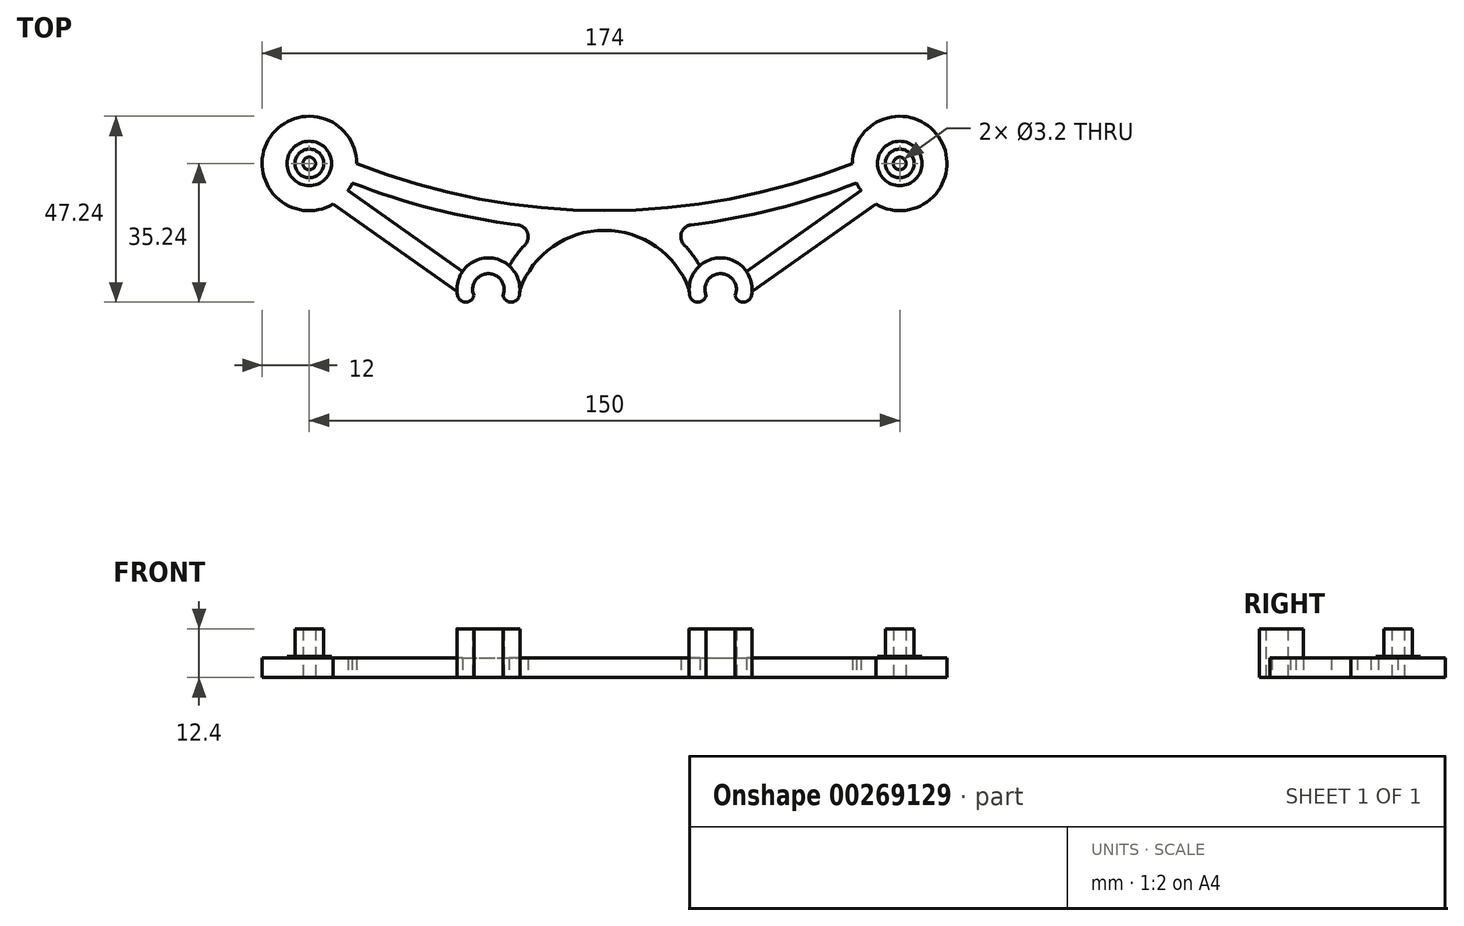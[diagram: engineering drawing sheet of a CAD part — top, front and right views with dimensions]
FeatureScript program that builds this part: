
annotation { "Feature Type Name" : "Feature", "Feature Type Description" : "" }
export const myFeature = defineFeature(function(context is Context, id is Id, definition is map)
    precondition{}
    {
        {
            var Q0;
            Q0=qCreatedBy(makeId("Top.planeOp"),FACE);
            var sketch = newSketch(context, id + "F0", { "sketchPlane" : qUnion([Q0])});
            skCircle(sketch, "E0", {"center": v(-75, 32) * mm, "radius": 1.6 * mm});
            skCircle(sketch, "E1", {"center": v(75, 32) * mm, "radius": 1.6 * mm});
            skCircle(sketch, "E2", {"center": v(29.5, 0) * mm, "radius": 4 * mm, "construction": true});
            skCircle(sketch, "E3", {"center": v(-29.5, 0) * mm, "radius": 4 * mm, "construction": true});
            skLineSegment(sketch, "E4", {"start": v(-29.5, 0) * mm, "end": v(29.5, 0) * mm, "construction": true});
            skPoint(sketch, "E5", {"position": v(0, 0) * mm});
            skLineSegment(sketch, "E6", {"start": v(-75, 32) * mm, "end": v(75, 32) * mm, "construction": true});
            skPoint(sketch, "E7", {"position": v(0, 32) * mm});
            skCircle(sketch, "E8", {"center": v(-75, 32) * mm, "radius": 3.65 * mm, "construction": true});
            skCircle(sketch, "E9", {"center": v(75, 32) * mm, "radius": 3.65 * mm, "construction": true});
            skCircle(sketch, "E10", {"center": v(75, 32) * mm, "radius": 12 * mm, "construction": true});
            skCircle(sketch, "E11", {"center": v(-75, 32) * mm, "radius": 12 * mm, "construction": true});
            skArc(sketch, "E12", {"start": v(-33.2, -1.53) * mm, "mid": v(-29.5, 4) * mm, "end": v(-25.8, -1.53) * mm});
            skLineSegment(sketch, "E13", {"start": v(-33.2, -1.53) * mm, "end": v(-25.8, -1.53) * mm, "construction": true});
            skArc(sketch, "E14", {"start": v(25.8, -1.53) * mm, "mid": v(29.5, 4) * mm, "end": v(33.2, -1.53) * mm});
            skLineSegment(sketch, "E15", {"start": v(25.8, -1.53) * mm, "end": v(33.2, -1.53) * mm, "construction": true});
            skArc(sketch, "E16", {"start": v(-37.35, -1.53) * mm, "mid": v(-29.5, 8) * mm, "end": v(-21.65, -1.53) * mm, "construction": true});
            skPoint(sketch, "E16.startSnap0", {"position": v(-29.5, -1.53) * mm});
            skArc(sketch, "E17", {"start": v(21.65, -1.53) * mm, "mid": v(29.5, 8) * mm, "end": v(37.35, -1.53) * mm, "construction": true});
            skArc(sketch, "E18", {"start": v(-37.35, -1.53) * mm, "mid": v(-35.27, -3.24) * mm, "end": v(-33.2, -1.53) * mm});
            skArc(sketch, "E19", {"start": v(-21.65, -1.53) * mm, "mid": v(-23.73, -3.24) * mm, "end": v(-25.8, -1.53) * mm});
            skArc(sketch, "E20", {"start": v(21.65, -1.53) * mm, "mid": v(23.73, -3.24) * mm, "end": v(25.8, -1.53) * mm});
            skArc(sketch, "E21", {"start": v(37.35, -1.53) * mm, "mid": v(35.27, -3.24) * mm, "end": v(33.2, -1.53) * mm});
            skArc(sketch, "E22", {"start": v(-63, 32) * mm, "mid": v(0, 20) * mm, "end": v(63, 32) * mm});
            skArc(sketch, "E23", {"start": v(21.5, 0) * mm, "mid": v(0, 15) * mm, "end": v(-21.5, 0) * mm});
            skArc(sketch, "E24.0", {"start": v(-64.07, 27.05) * mm, "mid": v(-43.37, 20.42) * mm, "end": v(-22.01, 16.38) * mm});
            skLineSegment(sketch, "E25", {"start": v(-37.48, -0.5) * mm, "end": v(37.48, -0.5) * mm, "construction": true});
            skLineSegment(sketch, "E26", {"start": v(-75, 20) * mm, "end": v(75, 20) * mm, "construction": true});
            skArc(sketch, "E27.trimOffspring", {"start": v(-20.21, 11.33) * mm, "mid": v(-22.37, 8.78) * mm, "end": v(-24.2, 6) * mm});
            skArc(sketch, "E28.trimOffspring", {"start": v(22.01, 16.38) * mm, "mid": v(43.37, 20.42) * mm, "end": v(64.07, 27.05) * mm});
            skArc(sketch, "E29.filletArc", {"start": v(22.01, 16.38) * mm, "mid": v(19.56, 14.4) * mm, "end": v(20.21, 11.33) * mm});
            skArc(sketch, "E30.filletArc", {"start": v(-20.21, 11.33) * mm, "mid": v(-19.56, 14.4) * mm, "end": v(-22.01, 16.38) * mm});
            skArc(sketch, "E31", {"start": v(63, 32) * mm, "mid": v(83.49, 40.49) * mm, "end": v(75, 20) * mm});
            skArc(sketch, "E32", {"start": v(-63, 32) * mm, "mid": v(-83.49, 40.49) * mm, "end": v(-75, 20) * mm});
            skArc(sketch, "E33", {"start": v(-37.35, -1.53) * mm, "mid": v(-37.44, -1.02) * mm, "end": v(-37.48, -0.5) * mm});
            skArc(sketch, "E34", {"start": v(37.35, -1.53) * mm, "mid": v(37.44, -1.02) * mm, "end": v(37.48, -0.5) * mm});
            skArc(sketch, "E35", {"start": v(36.04, 4.6) * mm, "mid": v(30.43, 7.95) * mm, "end": v(24.2, 6) * mm});
            skArc(sketch, "E36", {"start": v(21.5, 0) * mm, "mid": v(21.54, -0.77) * mm, "end": v(21.65, -1.53) * mm});
            skArc(sketch, "E37", {"start": v(-36.04, 4.6) * mm, "mid": v(-30.43, 7.95) * mm, "end": v(-24.2, 6) * mm});
            skArc(sketch, "E38", {"start": v(-21.5, 0) * mm, "mid": v(-21.54, -0.77) * mm, "end": v(-21.65, -1.53) * mm});
            skArc(sketch, "E39.trimOffspring", {"start": v(24.2, 6) * mm, "mid": v(22.37, 8.78) * mm, "end": v(20.21, 11.33) * mm});
            skLineSegment(sketch, "E40", {"start": v(25.8, -1.53) * mm, "end": v(29.5, 0) * mm, "construction": true});
            skLineSegment(sketch, "E41", {"start": v(33.2, -1.53) * mm, "end": v(29.5, 0) * mm, "construction": true});
            skLineSegment(sketch, "E42", {"start": v(37.48, -0.5) * mm, "end": v(68.95, 21.63) * mm});
            skLineSegment(sketch, "E43", {"start": v(-37.48, -0.5) * mm, "end": v(-68.95, 21.63) * mm});
            skArc(sketch, "E44", {"start": v(-68.95, 21.63) * mm, "mid": v(-71.87, 20.42) * mm, "end": v(-75, 20) * mm});
            skArc(sketch, "E45", {"start": v(75, 20) * mm, "mid": v(71.87, 20.42) * mm, "end": v(68.95, 21.63) * mm});
            skLineSegment(sketch, "E46", {"start": v(75, 32) * mm, "end": v(29.5, 0) * mm, "construction": true});
            skLineSegment(sketch, "E47", {"start": v(65.18, 25.1) * mm, "end": v(36.04, 4.6) * mm});
            skLineSegment(sketch, "E48", {"start": v(-36.04, 4.6) * mm, "end": v(-65.18, 25.1) * mm});
            skLineSegment(sketch, "E49", {"start": v(-75, 32) * mm, "end": v(-29.5, 0) * mm, "construction": true});
            skArc(sketch, "E50", {"start": v(-64.07, 27.05) * mm, "mid": v(-64.58, 26.05) * mm, "end": v(-65.18, 25.1) * mm});
            skArc(sketch, "E51", {"start": v(65.18, 25.1) * mm, "mid": v(64.58, 26.05) * mm, "end": v(64.07, 27.05) * mm});
            skSolve(sketch);
        }
        {
            var Q0;
            Q0 = qSketchRegion(id + "F0", true);
            extrude(context, id + "F1", {"entities" : qUnion([Q0]), "depth" : 5 * mm});
        }
        {
            var Q0;
            Q0=makeQuery(id+"F1.opExtrude","CAP_FACE",FACE,{"disambiguationData":[OSD([sQuery(id+"F0.wireOp",EDGE,"E0"),sQuery(id+"F0.wireOp",EDGE,"E1"),sQuery(id+"F0.wireOp",EDGE,"E12"),sQuery(id+"F0.wireOp",EDGE,"E14"),sQuery(id+"F0.wireOp",EDGE,"E18"),sQuery(id+"F0.wireOp",EDGE,"E19"),sQuery(id+"F0.wireOp",EDGE,"E20"),sQuery(id+"F0.wireOp",EDGE,"E21"),sQuery(id+"F0.wireOp",EDGE,"E22"),sQuery(id+"F0.wireOp",EDGE,"E23"),sQuery(id+"F0.wireOp",EDGE,"E24.0"),sQuery(id+"F0.wireOp",EDGE,"E27.trimOffspring"),sQuery(id+"F0.wireOp",EDGE,"E28.trimOffspring"),sQuery(id+"F0.wireOp",EDGE,"E29.filletArc"),sQuery(id+"F0.wireOp",EDGE,"E30.filletArc"),sQuery(id+"F0.wireOp",EDGE,"E31"),sQuery(id+"F0.wireOp",EDGE,"E32"),sQuery(id+"F0.wireOp",EDGE,"E33"),sQuery(id+"F0.wireOp",EDGE,"E34"),sQuery(id+"F0.wireOp",EDGE,"E35"),sQuery(id+"F0.wireOp",EDGE,"E36"),sQuery(id+"F0.wireOp",EDGE,"E37"),sQuery(id+"F0.wireOp",EDGE,"E38"),sQuery(id+"F0.wireOp",EDGE,"E39.trimOffspring"),sQuery(id+"F0.wireOp",EDGE,"E42"),sQuery(id+"F0.wireOp",EDGE,"E43"),sQuery(id+"F0.wireOp",EDGE,"E44"),sQuery(id+"F0.wireOp",EDGE,"E45"),sQuery(id+"F0.wireOp",EDGE,"E47"),sQuery(id+"F0.wireOp",EDGE,"E48"),sQuery(id+"F0.wireOp",EDGE,"E50"),sQuery(id+"F0.wireOp",EDGE,"E51")])],"isStart":false});
            var sketch = newSketch(context, id + "F2", { "sketchPlane" : qUnion([Q0])});
            skCircle(sketch, "E52", {"center": v(-75, 32) * mm, "radius": 3.65 * mm, "construction": true});
            skCircle(sketch, "E53", {"center": v(75, 32) * mm, "radius": 3.65 * mm, "construction": true});
            skCircle(sketch, "E54", {"center": v(-75, 32) * mm, "radius": 1.6 * mm});
            skCircle(sketch, "E55", {"center": v(75, 32) * mm, "radius": 1.6 * mm});
            skCircle(sketch, "E56", {"center": v(-75, 32) * mm, "radius": 5.65 * mm});
            skCircle(sketch, "E57", {"center": v(75, 32) * mm, "radius": 5.65 * mm});
            skSolve(sketch);
        }
        {
            var Q0;
            Q0 = qSketchRegion(id + "F2", true);
            extrude(context, id + "F3", {"entities" : qUnion([Q0]), "operationType" : NewBodyOperationType.ADD, "depth" : .4 * mm});
        }
        {
            var Q0;
            Q0=makeQuery(id+"F3.opExtrude","CAP_FACE",FACE,{"disambiguationData":[OSD([sQuery(id+"F2.wireOp",EDGE,"E54"),sQuery(id+"F2.wireOp",EDGE,"E56")])],"isStart":false});
            var sketch = newSketch(context, id + "F4", { "sketchPlane" : qUnion([Q0])});
            skCircle(sketch, "E58", {"center": v(-75, 32) * mm, "radius": 1.6 * mm});
            skCircle(sketch, "E59", {"center": v(-75, 32) * mm, "radius": 3.65 * mm});
            skCircle(sketch, "E60", {"center": v(75, 32) * mm, "radius": 1.6 * mm});
            skCircle(sketch, "E61", {"center": v(75, 32) * mm, "radius": 3.65 * mm});
            skSolve(sketch);
        }
        {
            var Q0;
            Q0 = qSketchRegion(id + "F4", true);
            extrude(context, id + "F5", {"entities" : qUnion([Q0]), "operationType" : NewBodyOperationType.ADD, "depth" : 7 * mm});
        }
        {
            var Q0;
            Q0=makeQuery(id+"F1.opExtrude","CAP_FACE",FACE,{"disambiguationData":[OSD([sQuery(id+"F0.wireOp",EDGE,"E0"),sQuery(id+"F0.wireOp",EDGE,"E1"),sQuery(id+"F0.wireOp",EDGE,"E12"),sQuery(id+"F0.wireOp",EDGE,"E14"),sQuery(id+"F0.wireOp",EDGE,"E18"),sQuery(id+"F0.wireOp",EDGE,"E19"),sQuery(id+"F0.wireOp",EDGE,"E20"),sQuery(id+"F0.wireOp",EDGE,"E21"),sQuery(id+"F0.wireOp",EDGE,"E22"),sQuery(id+"F0.wireOp",EDGE,"E23"),sQuery(id+"F0.wireOp",EDGE,"E24.0"),sQuery(id+"F0.wireOp",EDGE,"E27.trimOffspring"),sQuery(id+"F0.wireOp",EDGE,"E28.trimOffspring"),sQuery(id+"F0.wireOp",EDGE,"E29.filletArc"),sQuery(id+"F0.wireOp",EDGE,"E30.filletArc"),sQuery(id+"F0.wireOp",EDGE,"E31"),sQuery(id+"F0.wireOp",EDGE,"E32"),sQuery(id+"F0.wireOp",EDGE,"E33"),sQuery(id+"F0.wireOp",EDGE,"E34"),sQuery(id+"F0.wireOp",EDGE,"E35"),sQuery(id+"F0.wireOp",EDGE,"E36"),sQuery(id+"F0.wireOp",EDGE,"E37"),sQuery(id+"F0.wireOp",EDGE,"E38"),sQuery(id+"F0.wireOp",EDGE,"E39.trimOffspring"),sQuery(id+"F0.wireOp",EDGE,"E42"),sQuery(id+"F0.wireOp",EDGE,"E43"),sQuery(id+"F0.wireOp",EDGE,"E44"),sQuery(id+"F0.wireOp",EDGE,"E45"),sQuery(id+"F0.wireOp",EDGE,"E47"),sQuery(id+"F0.wireOp",EDGE,"E48"),sQuery(id+"F0.wireOp",EDGE,"E50"),sQuery(id+"F0.wireOp",EDGE,"E51")])],"isStart":false});
            var sketch = newSketch(context, id + "F6", { "sketchPlane" : qUnion([Q0])});
            skArc(sketch, "E62", {"start": v(-37.35, -1.53) * mm, "mid": v(-29.5, 8) * mm, "end": v(-21.65, -1.53) * mm});
            skArc(sketch, "E63", {"start": v(21.65, -1.53) * mm, "mid": v(29.5, 8) * mm, "end": v(37.35, -1.53) * mm});
            skArc(sketch, "E64", {"start": v(-33.2, -1.53) * mm, "mid": v(-29.5, 4) * mm, "end": v(-25.8, -1.53) * mm});
            skArc(sketch, "E65", {"start": v(25.8, -1.53) * mm, "mid": v(29.5, 4) * mm, "end": v(33.2, -1.53) * mm});
            skArc(sketch, "E66", {"start": v(37.35, -1.53) * mm, "mid": v(35.27, -3.24) * mm, "end": v(33.2, -1.53) * mm});
            skArc(sketch, "E67", {"start": v(21.65, -1.53) * mm, "mid": v(23.73, -3.24) * mm, "end": v(25.8, -1.53) * mm});
            skArc(sketch, "E68", {"start": v(-21.65, -1.53) * mm, "mid": v(-23.73, -3.24) * mm, "end": v(-25.8, -1.53) * mm});
            skArc(sketch, "E69", {"start": v(-37.35, -1.53) * mm, "mid": v(-35.27, -3.24) * mm, "end": v(-33.2, -1.53) * mm});
            skSolve(sketch);
        }
        {
            var Q0;
            Q0 = qSketchRegion(id + "F6", true);
            var Q1;
            Q1=makeQuery(id+"F5.opExtrude","CAP_FACE",FACE,{"disambiguationData":[OSD([sQuery(id+"F4.wireOp",EDGE,"E58"),sQuery(id+"F4.wireOp",EDGE,"E59")])],"isStart":false});
            extrude(context, id + "F7", {"entities" : qUnion([Q0]), "operationType" : NewBodyOperationType.ADD, "endBound" : BoundingType.UP_TO_SURFACE, "endBoundEntityFace" : qUnion([Q1]), "depth" : 25 * mm});
        }
    });
